# Revit family: Grohe_ShowerSet_Rainshower_22119KF0
name_source: partatom
category: Plumbing Fixtures
units: mm (PartAtom-declared; Revit-internal decimal feet)

## family parameters
Cut with Voids When Loaded = No
Host = Face
OmniClass Number = 23.45.05.00
OmniClass Title = Sanitary Equipment
Part Type = Normal
Room Calculation Point = No
Round Connector Dimension = Use Diameter
Shared = No

## types (1)
- RAINSHOWER Shower Set (22119KF0)
    Assembly Code = D2010
    AssetType = Fixed
    BIMObjectName = Grohe_ShowerSet_Rainshower_22119KF0
    CO2NeutralProduction = GROHE is one of the first leading manufacturer within the sanitary industry having a CO2-neutral production.
    CW Connection = Yes
    ClassificationName = Uniclass2015
    ClassificationValue = Pr_40_20_87_75
    Color = Matt Black
    Cost = 0 $
    Default Elevation = 0 mm  [stored 0 ft]
    Description = RAINSHOWER Shower Set
    DimensionsDocumentLink = https://cdn.cloud.grohe.com
    DocumentationCertificates = https://www.bimstore.co
    DocumentationInstallationGuide = https://www.bimstore.co
    DocumentationLiterature = https://www.bimstore.co
    DocumentationMaintenance = https://www.bimstore.co
    DocumentationTechnical = https://www.bimstore.co
    DurationUnit = Years
    EF000008 = 317 mm
    EF000040 = 1118 mm
    EF000049 = 472 mm
    EF000551 = 310 mm
    EF000634 = 0.0 Pa
    EF001707 = 70 °C
    EF002169 = Brass
    EF002286 = External thread
    EF002671 = Other
    EF003454 = FALSE
    EF003829 = FALSE
    EF005084 = Wall
    EF006009 = TRUE
    EF006013 = FALSE
    EF006974 = Thermostatic
    EF020103 = FALSE
    EF020785 = 1/2 inch
    EF021457 = FALSE
    EF021607 = FALSE
    EF021720 = TRUE
    EF021760 = TRUE
    EF022168 = TRUE
    EF022284 = FALSE
    EF023051 = Mechanical
    EF023061 = 0.0 Pa
    EF023686 = not applicable
    EF023957 = TRUE
    EF024792 = FALSE
    EF024885 = TRUE
    EF024921 = FALSE
    EF025090 = FALSE
    EF025091 = FALSE
    EF025092 = 0
    EF025093 = not applicable
    EF025094 = 1750
    EF025095 = not applicable
    EF025096 = TRUE
    EF025097 = 0.0 L/s
    EFSE0002 = TRUE
    Ecojoy = No
    ExpectedLife = 0
    FullRecyclabilityOfPlastic = All plastic components are fully recyclable
    GROHESocialCommittment = green.grohe.com/social_engagement
    GROHESustainability = green.grohe.com
    HW Connection = Yes
    IfcExportAs = IfcPipeFitting
    IfcExportType = IfcPipeFittingType
    Keynote = N13
    Manufacturer = Grohe
    ManufacturerName = Grohe
    Model = RAINSHOWER Shower Set
    ModelNumber = 22119KF0
    ModelReference = RAINSHOWER Shower Set
    NBSDescription = Shower fittings package
    NBSObjectName = Grohe - Shower fittings package
    NBSReference = 45-35-70/330
    NominalDepth = 0 mm  [stored 0 ft]
    NominalHeight = 0 mm  [stored 0 ft]
    NominalLength = 0 mm  [stored 0 ft]
    PQDiagramLink = https://cdn.cloud.grohe.com
    PrimaryMaterial = Grohe_MattBlack
    ProductDescription = consisting of:

horizontal swivable 450 mm shower arm

exposed thermostat with Aquadimmer function

allows change between:

head shower Rainshower Mono 310

with ball joint, rotation angle ± 15°

hand shower Rainshower SmartActive 130 (22 127 KF0)

adjustable in height with gliding element including performance grip

Silverflex shower hose 1750 mm (28 388)

GROHE TurboStat compact cartridge with wax thermoelement

GROHE SafeStop safety button at 38°C

GROHE SafeStop Plus optional temperature limiter at 43°C included

GROHE CoolTouch no risk of scalding

GROHE DreamSpray perfect spray pattern

GROHE SmartTip showering spray selection via push of a ring

GROHE Long-Life Shine finish

GROHE Water Saving 9.5 l/min flow limiter

GROHE FastFixation upper bracket adjustable

SpeedClean anti-limescale system

suitable for instantaneous heaters from 18 kW/h

minimum flow rate 7 l/min
    ProductNumber = 22119KF0
    ProductPageURL = https://www.grohe.co.uk
    ProductShortText = Rainshower System Shower system with thermostat for wall mounting
    ProductType = Shower System
    ProductionYear = 2023
    SustainabilityAward = green.grohe.com/awards
    SustainabilityReport = green.grohe.com/reporting
    TPIDocumentLink = https://cdn.cloud.grohe.com
    Type Comments = RAINSHOWER Shower Set
    TypeName = RAINSHOWER Shower Set
    URL = https://www.grohe.co.uk
    Vent Connection = No
    WarrantyDurationLabor = 0
    WarrantyDurationParts = 0
    WarrantyDurationUnit = Years
    Waste Connection = No
    _BSBibleVersion = 17
    _BimSpecGuid = 0
    _CurrentRevision = 1
    _DistributedBy = https://www.bimstore.co
    _ObjectUserGuide = https://www.bimstore.co

note: [stored X ft] marks values corroborated as IEEE doubles in the binary element streams (Revit-internal decimal feet)

## geometry (parser evidence)
native form markers: Sweep x3
no freeform markers — native parametric forms only
